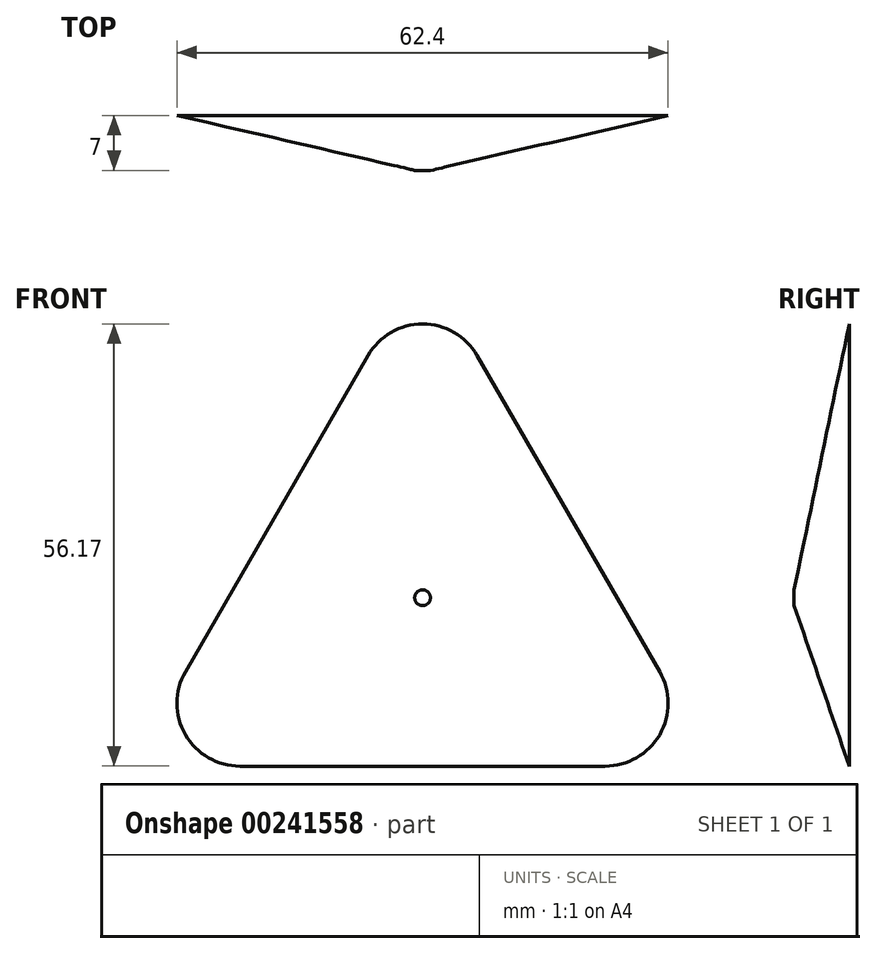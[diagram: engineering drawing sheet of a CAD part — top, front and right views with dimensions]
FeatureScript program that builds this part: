
annotation { "Feature Type Name" : "Feature", "Feature Type Description" : "" }
export const myFeature = defineFeature(function(context is Context, id is Id, definition is map)
    precondition{}
    {
        {
            var Q0;
            Q0=qCreatedBy(makeId("Front.planeOp"),FACE);
            cPlane(context, id + "F0", {"entities" : qUnion([Q0]), "cplaneType" : CPlaneType.OFFSET, "offset" : 7 * mm, "width" : 150 * mm, "height" : 150 * mm});
        }
        {
            var Q0;
            Q0=qCreatedBy(makeId("Front.planeOp"),FACE);
            var sketch = newSketch(context, id + "F1", { "sketchPlane" : qUnion([Q0])});
            skCircle(sketch, "E0.cCircle", {"center": v(0, 0) * mm, "radius": 42.78 * mm, "construction": true});
            skLineSegment(sketch, "E0.0", {"start": v(6.93, 30.78) * mm, "end": v(30.12, -9.4) * mm});
            skLineSegment(sketch, "E0.1", {"start": v(23.2, -21.4) * mm, "end": v(-23.2, -21.4) * mm});
            skLineSegment(sketch, "E0.2", {"start": v(-30.12, -9.4) * mm, "end": v(-6.93, 30.78) * mm});
            skPoint(sketch, "E1.visualSharp", {"position": v(0, 42.78) * mm});
            skArc(sketch, "E1.filletArc", {"start": v(6.93, 30.78) * mm, "mid": v(0, 34.78) * mm, "end": v(-6.93, 30.78) * mm});
            skPoint(sketch, "E2.visualSharp", {"position": v(-37.05, -21.4) * mm});
            skArc(sketch, "E2.filletArc", {"start": v(-30.12, -9.4) * mm, "mid": v(-30.12, -17.4) * mm, "end": v(-23.2, -21.4) * mm});
            skPoint(sketch, "E3.visualSharp", {"position": v(37.05, -21.4) * mm});
            skArc(sketch, "E3.filletArc", {"start": v(23.2, -21.4) * mm, "mid": v(30.12, -17.4) * mm, "end": v(30.12, -9.4) * mm});
            skSolve(sketch);
        }
        {
            var Q0;
            Q0=qCreatedBy(id+"F0.planeOp",FACE);
            var sketch = newSketch(context, id + "F2", { "sketchPlane" : qUnion([Q0])});
            skCircle(sketch, "E4", {"center": v(0, 0) * mm, "radius": 1 * mm});
            skSolve(sketch);
        }
        {
            var Q0;
            Q0 = qSketchRegion(id + "F1", true);
            var Q1;
            Q1 = qSketchRegion(id + "F2", true);
            loft(context, id + "F3", {"sheetProfilesArray" : [{ "sheetProfileEntities" : qUnion([Q0]) }, { "sheetProfileEntities" : qUnion([Q1]) }]});
        }
    });
